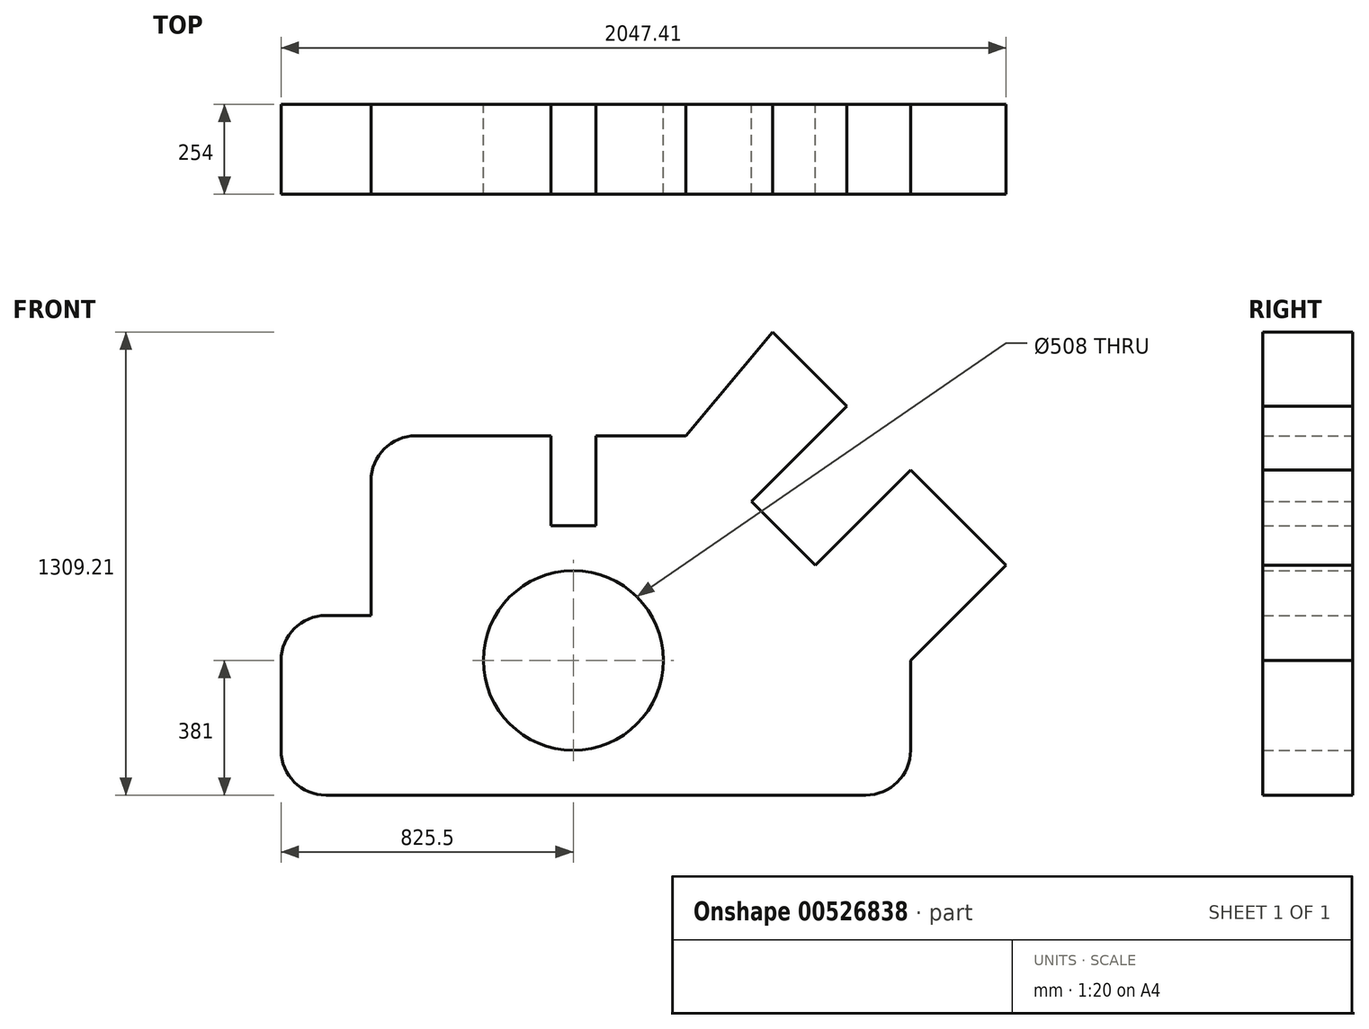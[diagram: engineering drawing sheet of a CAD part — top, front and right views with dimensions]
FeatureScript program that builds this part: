
annotation { "Feature Type Name" : "Feature", "Feature Type Description" : "" }
export const myFeature = defineFeature(function(context is Context, id is Id, definition is map)
    precondition{}
    {
        {
            var Q0;
            Q0=qCreatedBy(makeId("Front.planeOp"),FACE);
            var sketch = newSketch(context, id + "F0", { "sketchPlane" : qUnion([Q0])});
            skLineSegment(sketch, "E0", {"start": v(127, 0) * mm, "end": v(1651, 0) * mm});
            skLineSegment(sketch, "E1", {"start": v(1778, 127) * mm, "end": v(1778, 381) * mm});
            skLineSegment(sketch, "E2", {"start": v(0, 127) * mm, "end": v(0, 381) * mm});
            skPoint(sketch, "E3.visualSharp", {"position": v(0, 0) * mm});
            skArc(sketch, "E3.filletArc", {"start": v(0, 127) * mm, "mid": v(37.2, 37.2) * mm, "end": v(127, 0) * mm});
            skCircle(sketch, "E4", {"center": v(825.5, 381) * mm, "radius": 254 * mm});
            skLineSegment(sketch, "E5", {"start": v(127, 508) * mm, "end": v(254, 508) * mm});
            skPoint(sketch, "E6.visualSharp", {"position": v(0, 508) * mm});
            skArc(sketch, "E6.filletArc", {"start": v(127, 508) * mm, "mid": v(37.2, 470.8) * mm, "end": v(0, 381) * mm});
            skLineSegment(sketch, "E7", {"start": v(254, 508) * mm, "end": v(254, 889) * mm});
            skLineSegment(sketch, "E8", {"start": v(381, 1016) * mm, "end": v(762, 1016) * mm});
            skPoint(sketch, "E9.visualSharp", {"position": v(1778, 0) * mm});
            skArc(sketch, "E9.filletArc", {"start": v(1651, 0) * mm, "mid": v(1740.8, 37.2) * mm, "end": v(1778, 127) * mm});
            skPoint(sketch, "E10.visualSharp", {"position": v(254, 1016) * mm});
            skArc(sketch, "E10.filletArc", {"start": v(381, 1016) * mm, "mid": v(291.2, 978.8) * mm, "end": v(254, 889) * mm});
            skLineSegment(sketch, "E11", {"start": v(762, 1016) * mm, "end": v(762, 762) * mm});
            skLineSegment(sketch, "E12", {"start": v(762, 762) * mm, "end": v(889, 762) * mm});
            skLineSegment(sketch, "E13", {"start": v(889, 762) * mm, "end": v(889, 1016) * mm});
            skLineSegment(sketch, "E14", {"start": v(889, 1016) * mm, "end": v(1143, 1016) * mm});
            skLineSegment(sketch, "E15", {"start": v(1778, 381) * mm, "end": v(2047.4, 650.4) * mm});
            skLineSegment(sketch, "E16", {"start": v(2047.4, 650.4) * mm, "end": v(1778, 919.82) * mm});
            skLineSegment(sketch, "E17", {"start": v(1778, 919.82) * mm, "end": v(1508.6, 650.4) * mm});
            skLineSegment(sketch, "E18", {"start": v(1508.6, 650.4) * mm, "end": v(1328.99, 830.01) * mm});
            skLineSegment(sketch, "E19", {"start": v(1328.99, 830.01) * mm, "end": v(1598.4, 1099.42) * mm});
            skLineSegment(sketch, "E20", {"start": v(1598.4, 1099.42) * mm, "end": v(1388.6, 1309.21) * mm});
            skLineSegment(sketch, "E21", {"start": v(1143, 1016) * mm, "end": v(1388.6, 1309.21) * mm});
            skSolve(sketch);
        }
        {
            var Q0;
            Q0=makeQuery(id+"F0.imprint","IMPRINT",FACE,{"disambiguationData":[TD([[makeQuery(id+"F0.imprint","IMPRINT",EDGE,{"derivedFrom":sQuery(id+"F0.wireOp",EDGE,"E0")}),1.0]])]});
            extrude(context, id + "F1", {"entities" : qUnion([Q0]), "depth" : 254 * mm, "offsetDistance" : 25.4 * mm});
        }
    });
